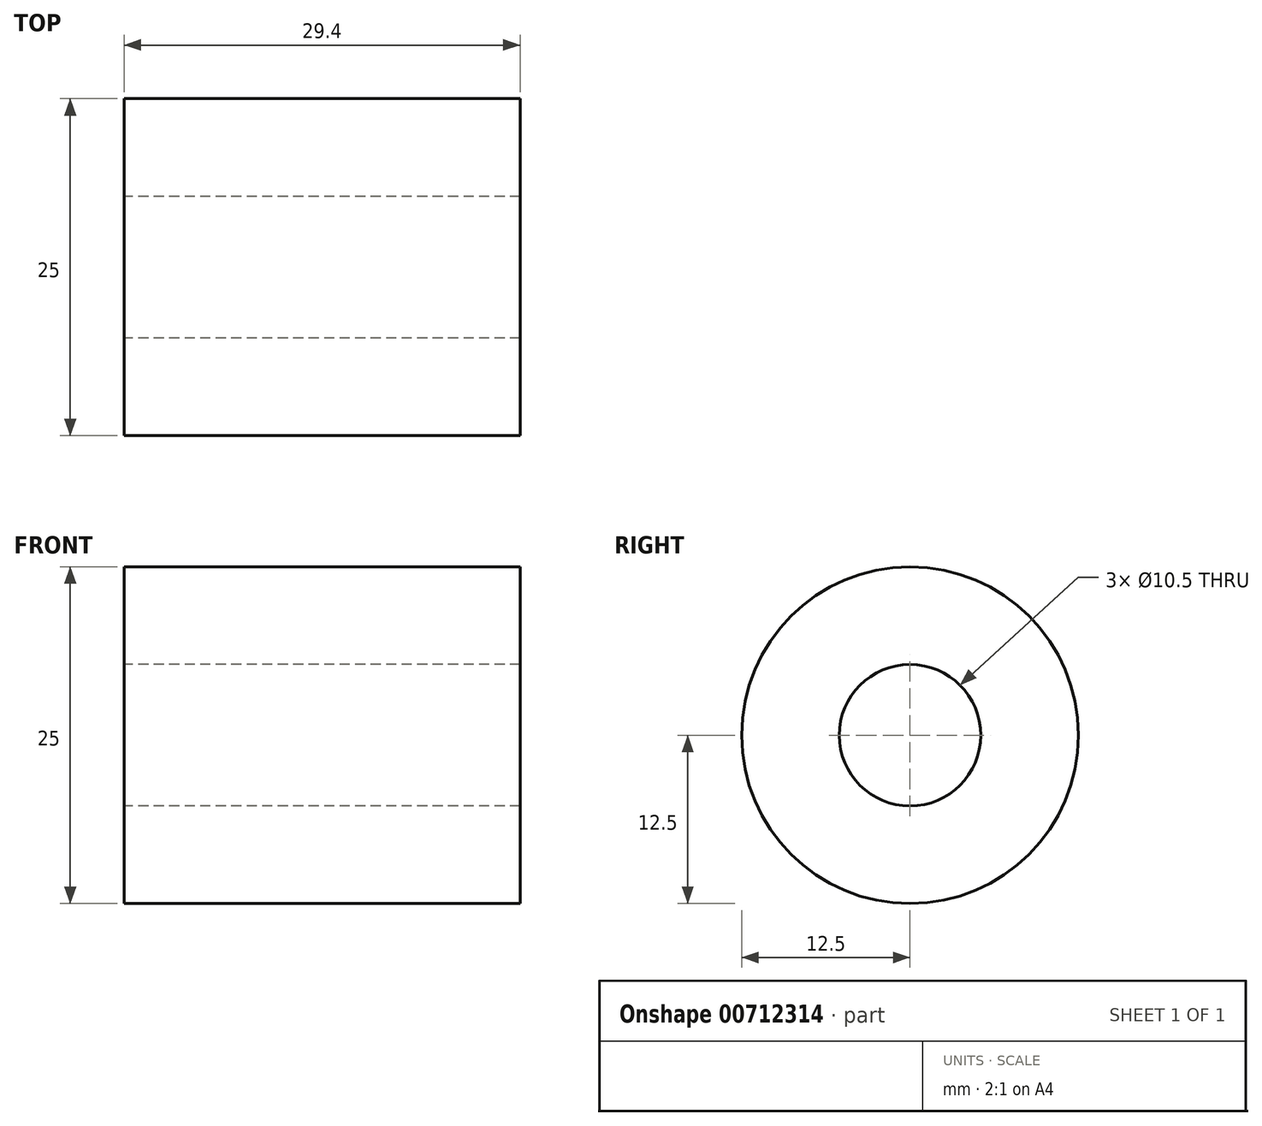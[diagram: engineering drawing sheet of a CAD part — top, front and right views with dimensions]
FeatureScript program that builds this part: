
annotation { "Feature Type Name" : "Feature", "Feature Type Description" : "" }
export const myFeature = defineFeature(function(context is Context, id is Id, definition is map)
    precondition{}
    {
        {
            var Q0;
            Q0=qCreatedBy(makeId("Right.planeOp"),FACE);
            var sketch = newSketch(context, id + "F0", { "sketchPlane" : qUnion([Q0])});
            skCircle(sketch, "E0", {"center": v(0, 0) * mm, "radius": 12.5 * mm});
            skCircle(sketch, "E1", {"center": v(0, 0) * mm, "radius": 5.25 * mm});
            skSolve(sketch);
        }
        {
            var Q0;
            Q0=qSketchRegion(id+"F0",true);
            extrude(context, id + "F1", {"entities" : qUnion([Q0]), "depth" : 29.4 * mm, "offsetDistance" : 25 * mm});
        }
    });
